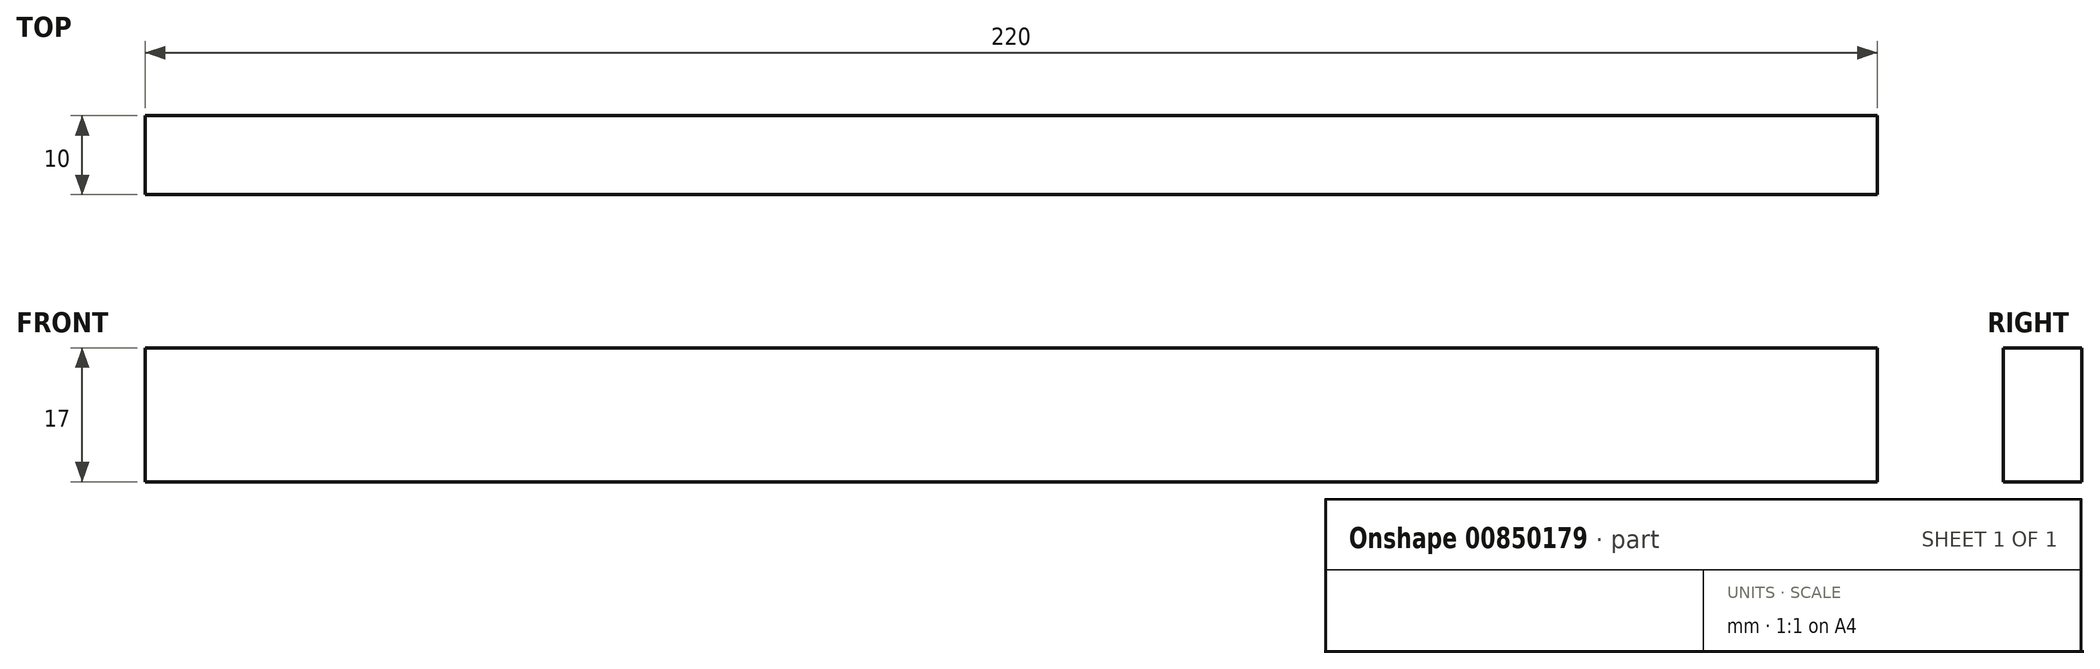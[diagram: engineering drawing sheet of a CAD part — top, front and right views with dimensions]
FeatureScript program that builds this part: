
annotation { "Feature Type Name" : "Feature", "Feature Type Description" : "" }
export const myFeature = defineFeature(function(context is Context, id is Id, definition is map)
    precondition{}
    {
        {
            var Q0;
            Q0=qCreatedBy(makeId("Right.planeOp"),FACE);
            var sketch = newSketch(context, id + "F0", { "sketchPlane" : qUnion([Q0])});
            skLineSegment(sketch, "E0.bottom", {"start": v(-5, 8.5) * mm, "end": v(5, 8.5) * mm});
            skLineSegment(sketch, "E0.top", {"start": v(-5, -8.5) * mm, "end": v(5, -8.5) * mm});
            skLineSegment(sketch, "E0.left", {"start": v(-5, 8.5) * mm, "end": v(-5, -8.5) * mm});
            skLineSegment(sketch, "E0.right", {"start": v(5, 8.5) * mm, "end": v(5, -8.5) * mm});
            skSolve(sketch);
        }
        {
            var Q0;
            Q0 = qSketchRegion(id + "F0", true);
            extrude(context, id + "F1", {"entities" : qUnion([Q0]), "depth" : 220 * mm, "offsetDistance" : 25 * mm});
        }
    });
